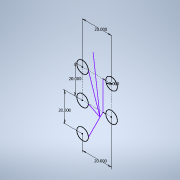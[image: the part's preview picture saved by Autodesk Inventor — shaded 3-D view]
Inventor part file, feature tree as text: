
AUTODESK INVENTOR PART (.ipt)
format: ipt  version: 2021.2 (Build 252289000, 289)  size: 95,744 bytes
history: native  units: in
note: dims shown in document units (in); Inventor stores cm internally (conversion verified against a paired STEP export)
features: sketch x1
ambient origin geometry x8: Origin, YZ Plane, XZ Plane, XY Plane, X Axis, Y Axis, Z Axis, Center Point
feature tree (1):
  sketch  "Sketch2"  dims[d9=20.0in d10=20.0in d11=8.0in d12=20.0in d13=20.0in]
